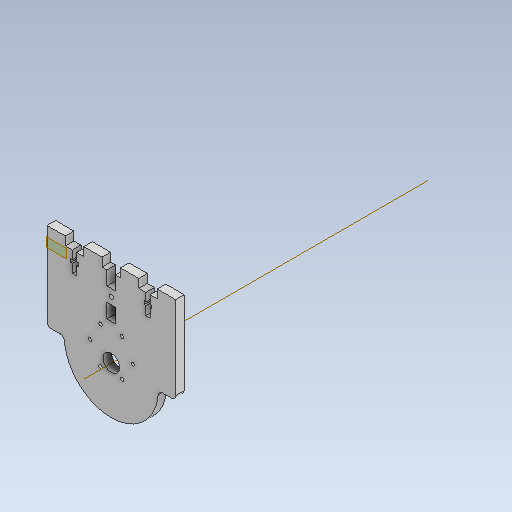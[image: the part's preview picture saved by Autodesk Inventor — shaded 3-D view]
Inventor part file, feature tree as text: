
AUTODESK INVENTOR PART (.ipt)
format: ipt  version: 2021.1 (Build 251245010, 245A)  size: 211,968 bytes
history: native  units: mm
features: other x8, reference x4, extrude x2, sketch x1
ambient origin geometry x8: Origin, YZ Plane, XZ Plane, XY Plane, X Axis, Y Axis, Z Axis, Center Point
bodies: Body1 (feature_tree)
feature tree (15):
  other  "Твердое тело1"
  other  "РабПлоскость1"
  sketch  "Эскиз1"
  other  "РабОсь1"
  extrude  "Выдавливание1"  Depth=57.0mm
  extrude  "Выдавливание2"  Depth=34.0mm
  reference  "Ссылка1"
  reference  "Ссылка2"
  reference  "Ссылка3"
  reference  "Ссылка4"
  other  "РабПлоскость2"
  other  "<userpath>\Documents\Savka\3d\Korp.iam"
  other  "Korp.iam"
  other  "Korpus 3:1"
  other  "Korpus:1"
